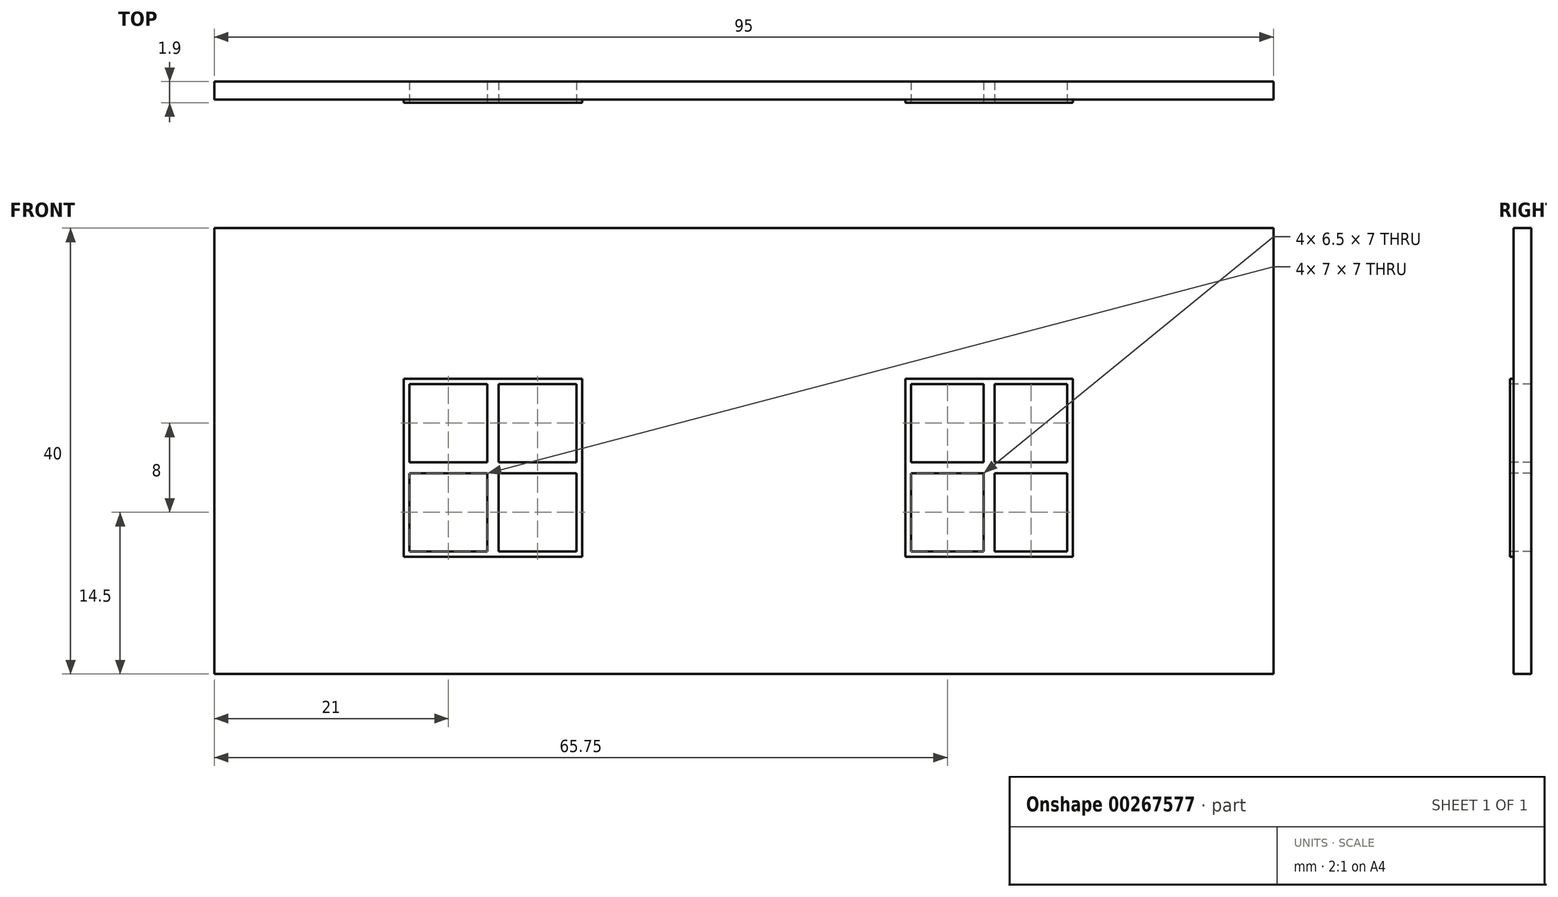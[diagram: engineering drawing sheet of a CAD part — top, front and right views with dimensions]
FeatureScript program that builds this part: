
annotation { "Feature Type Name" : "Feature", "Feature Type Description" : "" }
export const myFeature = defineFeature(function(context is Context, id is Id, definition is map)
    precondition{}
    {
        {
            var Q0;
            Q0=qCreatedBy(makeId("Top.planeOp"),FACE);
            var sketch = newSketch(context, id + "F0", { "sketchPlane" : qUnion([Q0])});
            skLineSegment(sketch, "E0.bottom", {"start": v(-47.5, 0.8) * mm, "end": v(47.5, 0.8) * mm});
            skLineSegment(sketch, "E0.top", {"start": v(-47.5, -0.8) * mm, "end": v(47.5, -0.8) * mm});
            skLineSegment(sketch, "E0.left", {"start": v(-47.5, 0.8) * mm, "end": v(-47.5, -0.8) * mm});
            skLineSegment(sketch, "E0.right", {"start": v(47.5, 0.8) * mm, "end": v(47.5, -0.8) * mm});
            skPoint(sketch, "E0.middle", {"position": v(0, 0) * mm});
            skSolve(sketch);
        }
        {
            var Q0;
            Q0 = qSketchRegion(id + "F0", true);
            extrude(context, id + "F1", {"entities" : qUnion([Q0]), "depth" : 40 * mm});
        }
        {
            var Q0;
            Q0=makeQuery(id+"F1.opExtrude","SWEPT_FACE",FACE,{"disambiguationData":[OSD([sQuery(id+"F0.wireOp",EDGE,"E0.top")])]});
            var sketch = newSketch(context, id + "F2", { "sketchPlane" : qUnion([Q0])});
            skLineSegment(sketch, "E1.bottom", {"start": v(-30, 26) * mm, "end": v(-15, 26) * mm});
            skLineSegment(sketch, "E1.top", {"start": v(-30, 11) * mm, "end": v(-15, 11) * mm});
            skLineSegment(sketch, "E1.left", {"start": v(-30, 26) * mm, "end": v(-30, 11) * mm});
            skLineSegment(sketch, "E1.right", {"start": v(-15, 26) * mm, "end": v(-15, 11) * mm});
            skPoint(sketch, "E1.middle", {"position": v(-22.5, 18.5) * mm});
            skLineSegment(sketch, "E2.bottom", {"start": v(15, 26) * mm, "end": v(29, 26) * mm});
            skLineSegment(sketch, "E2.top", {"start": v(15, 11) * mm, "end": v(29, 11) * mm});
            skLineSegment(sketch, "E2.left", {"start": v(15, 26) * mm, "end": v(15, 11) * mm});
            skLineSegment(sketch, "E2.right", {"start": v(29, 26) * mm, "end": v(29, 11) * mm});
            skPoint(sketch, "E2.middle", {"position": v(22, 18.5) * mm});
            skSolve(sketch);
        }
        {
            var Q0;
            Q0 = qSketchRegion(id + "F2", true);
            extrude(context, id + "F3", {"entities" : qUnion([Q0]), "operationType" : NewBodyOperationType.REMOVE, "oppositeDirection" : true, "depth" : 25 * mm});
        }
        {
            var Q0;
            Q0=makeQuery(id+"F1.opExtrude","SWEPT_FACE",FACE,{"disambiguationData":[OSD([sQuery(id+"F0.wireOp",EDGE,"E0.top")])]});
            var sketch = newSketch(context, id + "F4", { "sketchPlane" : qUnion([Q0])});
            skLineSegment(sketch, "E3.0", {"start": v(-30.5, 26.5) * mm, "end": v(-30.5, 10.5) * mm});
            skLineSegment(sketch, "E3.1", {"start": v(-30.5, 26.5) * mm, "end": v(-14.5, 26.5) * mm});
            skLineSegment(sketch, "E3.2", {"start": v(-14.5, 26.5) * mm, "end": v(-14.5, 10.5) * mm});
            skLineSegment(sketch, "E3.3", {"start": v(-30.5, 10.5) * mm, "end": v(-14.5, 10.5) * mm});
            skLineSegment(sketch, "E4.0", {"start": v(14.5, 26.5) * mm, "end": v(29.5, 26.5) * mm});
            skLineSegment(sketch, "E4.1", {"start": v(14.5, 26.5) * mm, "end": v(14.5, 10.5) * mm});
            skLineSegment(sketch, "E4.2", {"start": v(14.5, 10.5) * mm, "end": v(29.5, 10.5) * mm});
            skLineSegment(sketch, "E4.3", {"start": v(29.5, 26.5) * mm, "end": v(29.5, 10.5) * mm});
            skSolve(sketch);
        }
        {
            var Q0;
            Q0=makeQuery(id+"F4.imprint","IMPRINT",FACE,{"disambiguationData":[TD([[makeQuery(id+"F4.imprint","IMPRINT",EDGE,{"derivedFrom":sQuery(id+"F4.wireOp",EDGE,"E3.0")}),1.0]])]});
            var Q1;
            Q1=makeQuery(id+"F4.imprint","IMPRINT",FACE,{"disambiguationData":[TD([[makeQuery(id+"F4.imprint","IMPRINT",EDGE,{"derivedFrom":sQuery(id+"F4.wireOp",EDGE,"E4.0")}),-1.0]])]});
            extrude(context, id + "F5", {"entities" : qUnion([Q0, Q1]), "operationType" : NewBodyOperationType.ADD, "depth" : 0.3 * mm});
        }
        {
            var Q0;
            {var subQ0=sQuery(id+"F2.wireOp",EDGE,"E1.top");Q0=makeQuery(id+"F5.boolean.opBoolean","MERGE",FACE,{"derivedFrom":[makeQuery(id+"F3.boolean.opBoolean","COPY",FACE,{"derivedFrom":makeQuery(id+"F3.opExtrude","SWEPT_FACE",FACE,{"disambiguationData":[OSD([subQ0])]})}),makeQuery(id+"F5.opExtrude","SWEPT_FACE",FACE,{"disambiguationData":[OSD([subQ0])]})]});}
            var sketch = newSketch(context, id + "F6", { "sketchPlane" : qUnion([Q0])});
            skLineSegment(sketch, "E5.bottom", {"start": v(-22, -1.1) * mm, "end": v(-23, -1.1) * mm});
            skLineSegment(sketch, "E5.top", {"start": v(-22, 0.8) * mm, "end": v(-23, 0.8) * mm});
            skLineSegment(sketch, "E5.left", {"start": v(-22, -1.1) * mm, "end": v(-22, 0.8) * mm});
            skLineSegment(sketch, "E5.right", {"start": v(-23, -1.1) * mm, "end": v(-23, 0.8) * mm});
            skPoint(sketch, "E5.middle", {"position": v(-22.5, -0.15) * mm});
            skLineSegment(sketch, "E6.bottom", {"start": v(22.5, 0.8) * mm, "end": v(21.5, 0.8) * mm});
            skLineSegment(sketch, "E6.top", {"start": v(22.5, -1.1) * mm, "end": v(21.5, -1.1) * mm});
            skLineSegment(sketch, "E6.left", {"start": v(22.5, 0.8) * mm, "end": v(22.5, -1.1) * mm});
            skLineSegment(sketch, "E6.right", {"start": v(21.5, 0.8) * mm, "end": v(21.5, -1.1) * mm});
            skPoint(sketch, "E6.middle", {"position": v(22, -0.15) * mm});
            skSolve(sketch);
        }
        {
            var Q0;
            Q0=makeQuery(id+"F6.imprint","IMPRINT",FACE,{"disambiguationData":[TD([[makeQuery(id+"F6.imprint","IMPRINT",EDGE,{"derivedFrom":sQuery(id+"F6.wireOp",EDGE,"E6.bottom")}),1.0]])]});
            var Q1;
            Q1=makeQuery(id+"F6.imprint","IMPRINT",FACE,{"disambiguationData":[TD([[makeQuery(id+"F6.imprint","IMPRINT",EDGE,{"derivedFrom":sQuery(id+"F6.wireOp",EDGE,"E5.bottom")}),1.0]])]});
            extrude(context, id + "F7", {"entities" : qUnion([Q0, Q1]), "operationType" : NewBodyOperationType.ADD, "endBound" : BoundingType.UP_TO_NEXT, "depth" : 25 * mm});
        }
        {
            var Q0;
            {var subQ0=sQuery(id+"F2.wireOp",EDGE,"E1.right");Q0=makeQuery(id+"F5.boolean.opBoolean","MERGE",FACE,{"derivedFrom":[makeQuery(id+"F3.boolean.opBoolean","COPY",FACE,{"derivedFrom":makeQuery(id+"F3.opExtrude","SWEPT_FACE",FACE,{"disambiguationData":[OSD([subQ0])]})}),makeQuery(id+"F5.opExtrude","SWEPT_FACE",FACE,{"disambiguationData":[OSD([subQ0])]})]});}
            var sketch = newSketch(context, id + "F8", { "sketchPlane" : qUnion([Q0])});
            skSolve(sketch);
        }
        {
            var Q0;
            {var subQ0=sQuery(id+"F2.wireOp",EDGE,"E1.right");Q0=makeQuery(id+"F8.imprint","IMPRINT",FACE,{"disambiguationData":[TD([[makeQuery(id+"F8.imprint","IMPRINT",EDGE,{"derivedFrom":makeQuery(id+"F5.opExtrude","CAP_EDGE",EDGE,{"disambiguationData":[OSD([subQ0])],"isStart":false})}),-1.0]])]});}
            var sketch = newSketch(context, id + "F9", { "sketchPlane" : qUnion([Q0])});
            skLineSegment(sketch, "E7.top", {"start": v(0.8, 18) * mm, "end": v(-0.8, 18) * mm});
            skLineSegment(sketch, "E7.right", {"start": v(-0.8, 19) * mm, "end": v(-0.8, 18) * mm});
            skPoint(sketch, "E7.middle", {"position": v(0, 18.5) * mm});
            skLineSegment(sketch, "E8", {"start": v(-0.8, 19) * mm, "end": v(1.1, 19) * mm});
            skLineSegment(sketch, "E9", {"start": v(1.1, 19) * mm, "end": v(1.1, 18) * mm});
            skLineSegment(sketch, "E10", {"start": v(1.1, 18) * mm, "end": v(0.8, 18) * mm});
            skSolve(sketch);
        }
        {
            var Q0;
            {var subQ0=sQuery(id+"F2.wireOp",EDGE,"E2.right");Q0=makeQuery(id+"F5.boolean.opBoolean","MERGE",FACE,{"derivedFrom":[makeQuery(id+"F3.boolean.opBoolean","COPY",FACE,{"derivedFrom":makeQuery(id+"F3.opExtrude","SWEPT_FACE",FACE,{"disambiguationData":[OSD([subQ0])]})}),makeQuery(id+"F5.opExtrude","SWEPT_FACE",FACE,{"disambiguationData":[OSD([subQ0])]})]});}
            var sketch = newSketch(context, id + "F10", { "sketchPlane" : qUnion([Q0])});
            skLineSegment(sketch, "E11.bottom", {"start": v(-0.8, 19) * mm, "end": v(1.1, 19) * mm});
            skLineSegment(sketch, "E11.top", {"start": v(-0.8, 18) * mm, "end": v(1.1, 18) * mm});
            skLineSegment(sketch, "E11.left", {"start": v(-0.8, 19) * mm, "end": v(-0.8, 18) * mm});
            skLineSegment(sketch, "E11.right", {"start": v(1.1, 19) * mm, "end": v(1.1, 18) * mm});
            skPoint(sketch, "E11.middle", {"position": v(0.15, 18.5) * mm});
            skSolve(sketch);
        }
        {
            var Q0;
            Q0=makeQuery(id+"F9.imprint","IMPRINT",FACE,{"disambiguationData":[TD([[makeQuery(id+"F9.imprint","IMPRINT",EDGE,{"derivedFrom":sQuery(id+"F9.wireOp",EDGE,"E7.top")}),-1.0]])]});
            var Q1;
            {var subQ0=sQuery(id+"F2.wireOp",EDGE,"E1.left");Q1=makeQuery(id+"F5.boolean.opBoolean","MERGE",FACE,{"derivedFrom":[makeQuery(id+"F3.boolean.opBoolean","COPY",FACE,{"derivedFrom":makeQuery(id+"F3.opExtrude","SWEPT_FACE",FACE,{"disambiguationData":[OSD([subQ0])]})}),makeQuery(id+"F5.opExtrude","SWEPT_FACE",FACE,{"disambiguationData":[OSD([subQ0])]})]});}
            extrude(context, id + "F11", {"entities" : qUnion([Q0]), "operationType" : NewBodyOperationType.ADD, "endBound" : BoundingType.UP_TO_SURFACE, "endBoundEntityFace" : qUnion([Q1]), "depth" : 15 * mm});
        }
        {
            var Q0;
            Q0=makeQuery(id+"F10.imprint","IMPRINT",FACE,{"disambiguationData":[TD([[makeQuery(id+"F10.imprint","IMPRINT",EDGE,{"derivedFrom":sQuery(id+"F10.wireOp",EDGE,"E11.bottom")}),-1.0]])]});
            var Q1;
            {var subQ0=sQuery(id+"F2.wireOp",EDGE,"E2.left");Q1=makeQuery(id+"F5.boolean.opBoolean","MERGE",FACE,{"derivedFrom":[makeQuery(id+"F3.boolean.opBoolean","COPY",FACE,{"derivedFrom":makeQuery(id+"F3.opExtrude","SWEPT_FACE",FACE,{"disambiguationData":[OSD([subQ0])]})}),makeQuery(id+"F5.opExtrude","SWEPT_FACE",FACE,{"disambiguationData":[OSD([subQ0])]})]});}
            extrude(context, id + "F12", {"entities" : qUnion([Q0]), "operationType" : NewBodyOperationType.ADD, "endBound" : BoundingType.UP_TO_SURFACE, "endBoundEntityFace" : qUnion([Q1]), "depth" : 25 * mm});
        }
    });
